# Revit family: Atlas_Sound_I128SYSM
name_source: partatom
category: Communication Devices
units: mm (PartAtom-declared; Revit-internal decimal feet)

## family parameters
Always vertical = No
Cut with Voids When Loaded = No
Maintain Annotation Orientation = No
Part Type = Normal
Room Calculation Point = No
Round Connector Dimension = Use Diameter
Shared = No
Work Plane-Based = Yes

## types (1)
- IP Enabled Loudspeakers
    100V Taps = 32.00 W
    70V Taps = 32.00 W
    Baffle Material = <By Category>
    Body Material = QF_Metal - Stainless - Polished
    Color = <By Category>
    Communication Ports = RJ-45 Female
    Cost = 1247.99 $
    Cost MSRP = 1247.99 $
    Coverage = 105° (2kHz Octave Band, -6dB Points
    Coverage Horizontal = 105.00°
    Coverage Vertical = 105.00°
    Default Elevation = 48 "
    Depth = 23.69 "
    Description = POE+ INDOOR 1’ X 2’ SUSPENDED CEILING MOUNT IP LOUDSPEAKER WITH PAGING MICROPHONE
    Dispersion Angle = 0.00°
    Enclosure Material = <By Category>
    Family Code (default) = LOUD SPEAKERS
    Frequency Response  = 86Hz - 15.5kHz
    Grill Material = QF_Plastic - Black - Fine Textured
    Height = 4.92 "
    IQ Category = SPEAKERS
    Impedance = 8
    Ingress Protection = IP-XX (Not Rated)
    Input Connectors = One Unbalanced Analog, Secured Screw Terminal Block, G.711, G.722 Capable
    Loudspeaker Level = 8Ω, 9W (802.3AF), 15W (802.3AT)
    Manufacturer = ATLAS SOUND
    Manufacturer URL = https://www.atlasied.com
    Market = Commercial, Higher Education, Emergency
    MasterFormat = 27 41 13
    MaterFormat Title = SPEAKERS
    Model = I128SYSM+
    Mount Material = QF_Plastic - White - Smooth
    Mounting/Rigging Provisions = Lay-In Into A Reflected Ceiling Grid
    OmniClass Number = 23-37 17 13 19
    OmniClass Title = SPEAKERS
    Operation Mode = Self Powered
    Power Rating (RMS) = 15 Watts Max (802.3AT)
    Product Documentation Link = https://www.atlasied.com
    Product Page URL = https://www.atlasied.com
    Recommended Signal Processing = Built-In Processing
    SPL Max = 95
    Safety Agency Ratings = ETL Listed to Comply with UL-60950-1, and CAN/CSA-C22.2 No. 60950-1
    ScheduleType |RF| = AtlasIED Master
    Speaker Dispersion = 105.00°
    Speaker Type = S1
    Transformer Option = Yes
    URL = www.atlassound.com
    Vertical Symmetry = Yes
    Voltage AC = PoE or PoE+ and External 24VDC
    Warranty = 1 Year
    Weight Product = 10
    Width = 11.94 "

## geometry (parser evidence)
native form markers: Blend x4, Sweep x3
no freeform markers — native parametric forms only
